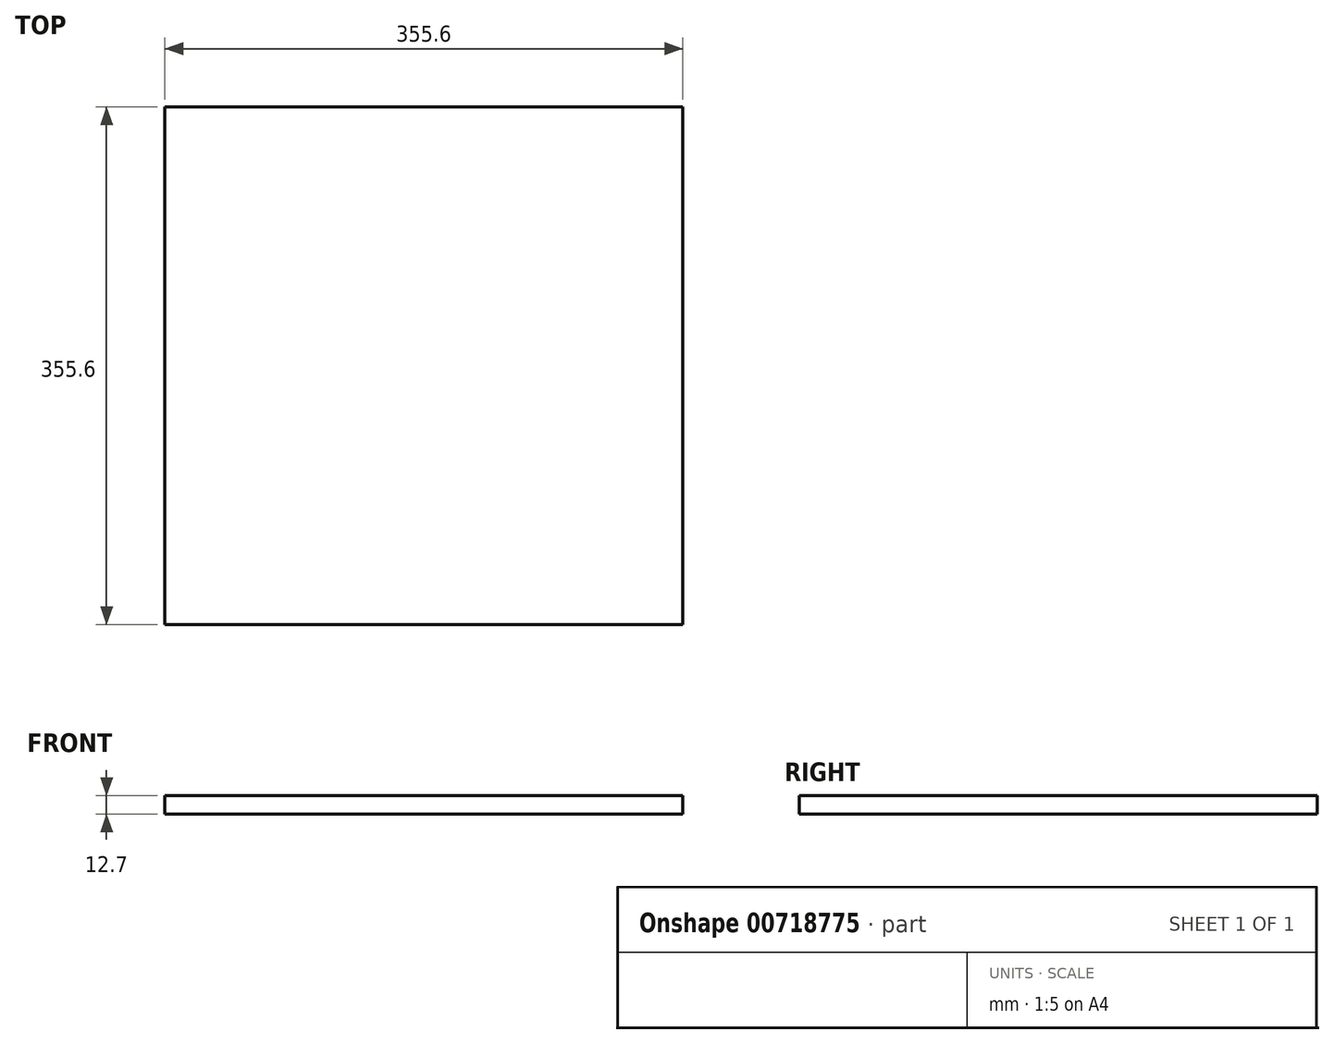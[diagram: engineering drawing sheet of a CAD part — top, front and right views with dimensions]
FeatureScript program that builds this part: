
annotation { "Feature Type Name" : "Feature", "Feature Type Description" : "" }
export const myFeature = defineFeature(function(context is Context, id is Id, definition is map)
    precondition{}
    {
        {
            var Q0;
            Q0=qCreatedBy(makeId("Top.planeOp"),FACE);
            var sketch = newSketch(context, id + "F0", { "sketchPlane" : qUnion([Q0])});
            skLineSegment(sketch, "E0.bottom", {"start": v(-171.78, 150.27) * mm, "end": v(183.82, 150.27) * mm});
            skLineSegment(sketch, "E0.top", {"start": v(-171.78, -205.33) * mm, "end": v(183.82, -205.33) * mm});
            skLineSegment(sketch, "E0.left", {"start": v(-171.78, 150.27) * mm, "end": v(-171.78, -205.33) * mm});
            skLineSegment(sketch, "E0.right", {"start": v(183.82, 150.27) * mm, "end": v(183.82, -205.33) * mm});
            skSolve(sketch);
        }
        {
            var Q0;
            Q0=makeQuery(id+"F0.imprint","IMPRINT",FACE,{"disambiguationData":[TD([[makeQuery(id+"F0.imprint","IMPRINT",EDGE,{"derivedFrom":sQuery(id+"F0.wireOp",EDGE,"E0.bottom")}),-1.0]])]});
            extrude(context, id + "F1", {"entities" : qUnion([Q0]), "depth" : 12.7 * mm, "offsetDistance" : 25.4 * mm});
        }
    });
